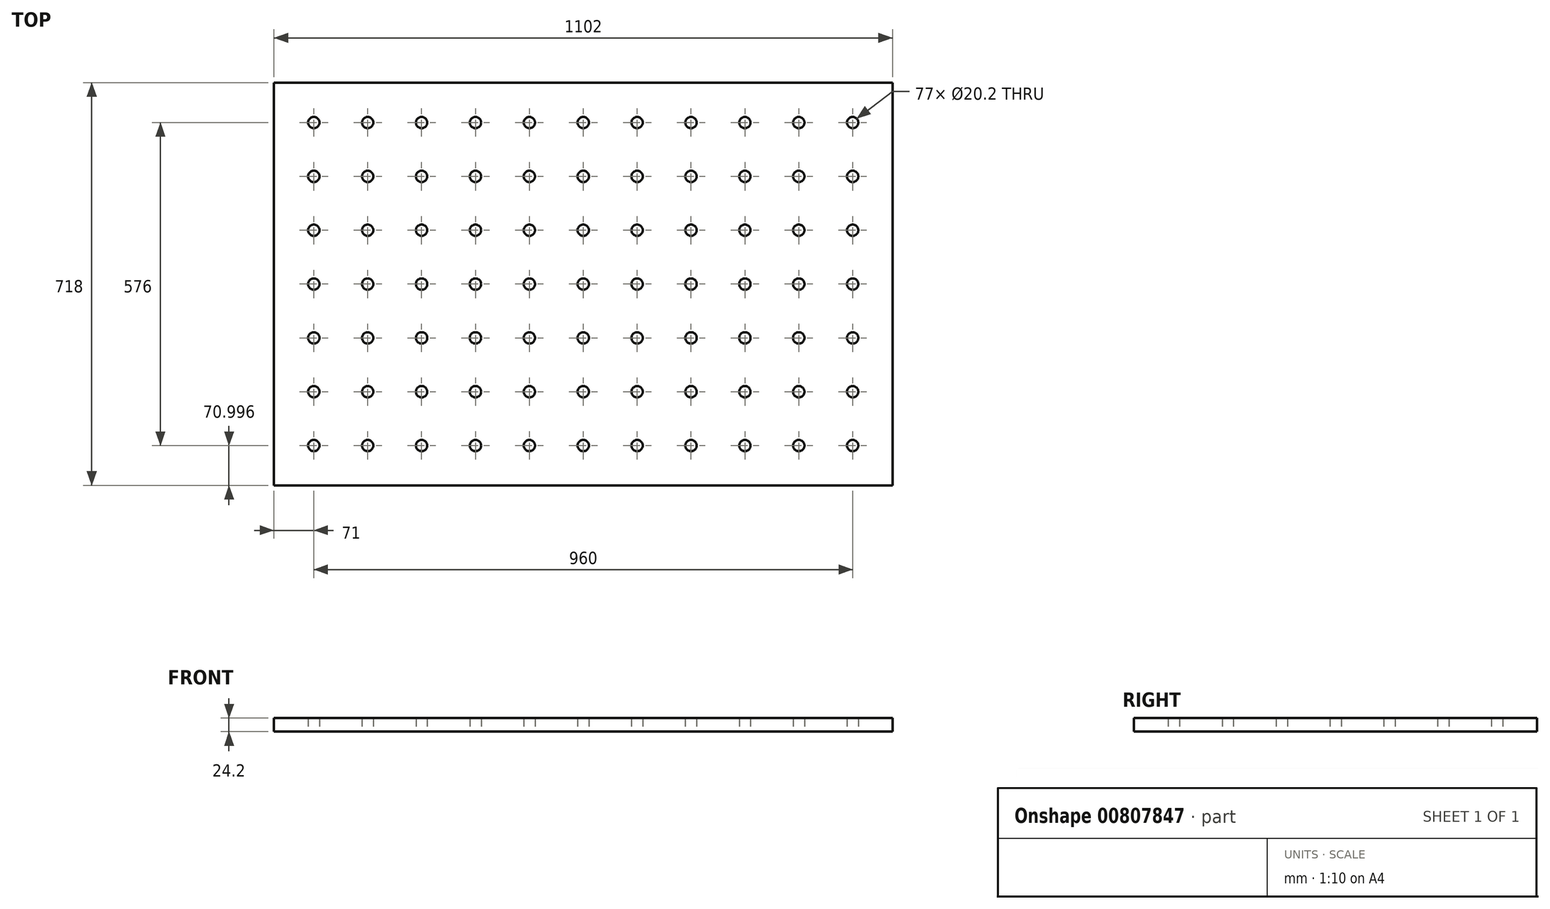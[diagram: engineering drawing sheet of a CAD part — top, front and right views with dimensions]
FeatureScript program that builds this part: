
annotation { "Feature Type Name" : "Feature", "Feature Type Description" : "" }
export const myFeature = defineFeature(function(context is Context, id is Id, definition is map)
    precondition{}
    {
        {
            var Q0;
            Q0=qCreatedBy(makeId("Top.planeOp"),FACE);
            var sketch = newSketch(context, id + "F0", { "sketchPlane" : qUnion([Q0])});
            skLineSegment(sketch, "E0.bottom", {"start": v(-588.77, 386.05) * mm, "end": v(513.23, 386.05) * mm});
            skLineSegment(sketch, "E0.top", {"start": v(-588.77, -331.95) * mm, "end": v(513.23, -331.95) * mm});
            skLineSegment(sketch, "E0.left", {"start": v(-588.77, 386.05) * mm, "end": v(-588.77, -331.95) * mm});
            skLineSegment(sketch, "E0.right", {"start": v(513.23, 386.05) * mm, "end": v(513.23, -331.95) * mm});
            skCircle(sketch, "E1", {"center": v(-517.77, 315.05) * mm, "radius": 10.1 * mm});
            skCircle(sketch, "E2.0.1.0", {"center": v(-517.77, 219.05) * mm, "radius": 10.1 * mm});
            skCircle(sketch, "E2.0.2.0", {"center": v(-517.77, 123.05) * mm, "radius": 10.1 * mm});
            skCircle(sketch, "E2.0.3.0", {"center": v(-517.77, 27.05) * mm, "radius": 10.1 * mm});
            skCircle(sketch, "E2.0.4.0", {"center": v(-517.77, -68.95) * mm, "radius": 10.1 * mm});
            skCircle(sketch, "E2.0.5.0", {"center": v(-517.77, -164.95) * mm, "radius": 10.1 * mm});
            skCircle(sketch, "E2.0.6.0", {"center": v(-517.77, -260.95) * mm, "radius": 10.1 * mm});
            skCircle(sketch, "E2.1.0.0", {"center": v(-421.77, 315.05) * mm, "radius": 10.1 * mm});
            skCircle(sketch, "E2.1.1.0", {"center": v(-421.77, 219.05) * mm, "radius": 10.1 * mm});
            skCircle(sketch, "E2.1.2.0", {"center": v(-421.77, 123.05) * mm, "radius": 10.1 * mm});
            skCircle(sketch, "E2.1.3.0", {"center": v(-421.77, 27.05) * mm, "radius": 10.1 * mm});
            skCircle(sketch, "E2.1.4.0", {"center": v(-421.77, -68.95) * mm, "radius": 10.1 * mm});
            skCircle(sketch, "E2.1.5.0", {"center": v(-421.77, -164.95) * mm, "radius": 10.1 * mm});
            skCircle(sketch, "E2.1.6.0", {"center": v(-421.77, -260.95) * mm, "radius": 10.1 * mm});
            skCircle(sketch, "E2.2.0.0", {"center": v(-325.77, 315.05) * mm, "radius": 10.1 * mm});
            skCircle(sketch, "E2.2.1.0", {"center": v(-325.77, 219.05) * mm, "radius": 10.1 * mm});
            skCircle(sketch, "E2.2.2.0", {"center": v(-325.77, 123.05) * mm, "radius": 10.1 * mm});
            skCircle(sketch, "E2.2.3.0", {"center": v(-325.77, 27.05) * mm, "radius": 10.1 * mm});
            skCircle(sketch, "E2.2.4.0", {"center": v(-325.77, -68.95) * mm, "radius": 10.1 * mm});
            skCircle(sketch, "E2.2.5.0", {"center": v(-325.77, -164.95) * mm, "radius": 10.1 * mm});
            skCircle(sketch, "E2.2.6.0", {"center": v(-325.77, -260.95) * mm, "radius": 10.1 * mm});
            skCircle(sketch, "E2.3.0.0", {"center": v(-229.77, 315.05) * mm, "radius": 10.1 * mm});
            skCircle(sketch, "E2.3.1.0", {"center": v(-229.77, 219.05) * mm, "radius": 10.1 * mm});
            skCircle(sketch, "E2.3.2.0", {"center": v(-229.77, 123.05) * mm, "radius": 10.1 * mm});
            skCircle(sketch, "E2.3.3.0", {"center": v(-229.77, 27.05) * mm, "radius": 10.1 * mm});
            skCircle(sketch, "E2.3.4.0", {"center": v(-229.77, -68.95) * mm, "radius": 10.1 * mm});
            skCircle(sketch, "E2.3.5.0", {"center": v(-229.77, -164.95) * mm, "radius": 10.1 * mm});
            skCircle(sketch, "E2.3.6.0", {"center": v(-229.77, -260.95) * mm, "radius": 10.1 * mm});
            skCircle(sketch, "E2.4.0.0", {"center": v(-133.77, 315.05) * mm, "radius": 10.1 * mm});
            skCircle(sketch, "E2.4.1.0", {"center": v(-133.77, 219.05) * mm, "radius": 10.1 * mm});
            skCircle(sketch, "E2.4.2.0", {"center": v(-133.77, 123.05) * mm, "radius": 10.1 * mm});
            skCircle(sketch, "E2.4.3.0", {"center": v(-133.77, 27.05) * mm, "radius": 10.1 * mm});
            skCircle(sketch, "E2.4.4.0", {"center": v(-133.77, -68.95) * mm, "radius": 10.1 * mm});
            skCircle(sketch, "E2.4.5.0", {"center": v(-133.77, -164.95) * mm, "radius": 10.1 * mm});
            skCircle(sketch, "E2.4.6.0", {"center": v(-133.77, -260.95) * mm, "radius": 10.1 * mm});
            skCircle(sketch, "E2.5.0.0", {"center": v(-37.77, 315.05) * mm, "radius": 10.1 * mm});
            skCircle(sketch, "E2.5.1.0", {"center": v(-37.77, 219.05) * mm, "radius": 10.1 * mm});
            skCircle(sketch, "E2.5.2.0", {"center": v(-37.77, 123.05) * mm, "radius": 10.1 * mm});
            skCircle(sketch, "E2.5.3.0", {"center": v(-37.77, 27.05) * mm, "radius": 10.1 * mm});
            skCircle(sketch, "E2.5.4.0", {"center": v(-37.77, -68.95) * mm, "radius": 10.1 * mm});
            skCircle(sketch, "E2.5.5.0", {"center": v(-37.77, -164.95) * mm, "radius": 10.1 * mm});
            skCircle(sketch, "E2.5.6.0", {"center": v(-37.77, -260.95) * mm, "radius": 10.1 * mm});
            skCircle(sketch, "E2.6.0.0", {"center": v(58.23, 315.05) * mm, "radius": 10.1 * mm});
            skCircle(sketch, "E2.6.1.0", {"center": v(58.23, 219.05) * mm, "radius": 10.1 * mm});
            skCircle(sketch, "E2.6.2.0", {"center": v(58.23, 123.05) * mm, "radius": 10.1 * mm});
            skCircle(sketch, "E2.6.3.0", {"center": v(58.23, 27.05) * mm, "radius": 10.1 * mm});
            skCircle(sketch, "E2.6.4.0", {"center": v(58.23, -68.95) * mm, "radius": 10.1 * mm});
            skCircle(sketch, "E2.6.5.0", {"center": v(58.23, -164.95) * mm, "radius": 10.1 * mm});
            skCircle(sketch, "E2.6.6.0", {"center": v(58.23, -260.95) * mm, "radius": 10.1 * mm});
            skCircle(sketch, "E2.7.0.0", {"center": v(154.23, 315.05) * mm, "radius": 10.1 * mm});
            skCircle(sketch, "E2.7.1.0", {"center": v(154.23, 219.05) * mm, "radius": 10.1 * mm});
            skCircle(sketch, "E2.7.2.0", {"center": v(154.23, 123.05) * mm, "radius": 10.1 * mm});
            skCircle(sketch, "E2.7.3.0", {"center": v(154.23, 27.05) * mm, "radius": 10.1 * mm});
            skCircle(sketch, "E2.7.4.0", {"center": v(154.23, -68.95) * mm, "radius": 10.1 * mm});
            skCircle(sketch, "E2.7.5.0", {"center": v(154.23, -164.95) * mm, "radius": 10.1 * mm});
            skCircle(sketch, "E2.7.6.0", {"center": v(154.23, -260.95) * mm, "radius": 10.1 * mm});
            skCircle(sketch, "E2.8.0.0", {"center": v(250.23, 315.05) * mm, "radius": 10.1 * mm});
            skCircle(sketch, "E2.8.1.0", {"center": v(250.23, 219.05) * mm, "radius": 10.1 * mm});
            skCircle(sketch, "E2.8.2.0", {"center": v(250.23, 123.05) * mm, "radius": 10.1 * mm});
            skCircle(sketch, "E2.8.3.0", {"center": v(250.23, 27.05) * mm, "radius": 10.1 * mm});
            skCircle(sketch, "E2.8.4.0", {"center": v(250.23, -68.95) * mm, "radius": 10.1 * mm});
            skCircle(sketch, "E2.8.5.0", {"center": v(250.23, -164.95) * mm, "radius": 10.1 * mm});
            skCircle(sketch, "E2.8.6.0", {"center": v(250.23, -260.95) * mm, "radius": 10.1 * mm});
            skCircle(sketch, "E2.9.0.0", {"center": v(346.23, 315.05) * mm, "radius": 10.1 * mm});
            skCircle(sketch, "E2.9.1.0", {"center": v(346.23, 219.05) * mm, "radius": 10.1 * mm});
            skCircle(sketch, "E2.9.2.0", {"center": v(346.23, 123.05) * mm, "radius": 10.1 * mm});
            skCircle(sketch, "E2.9.3.0", {"center": v(346.23, 27.05) * mm, "radius": 10.1 * mm});
            skCircle(sketch, "E2.9.4.0", {"center": v(346.23, -68.95) * mm, "radius": 10.1 * mm});
            skCircle(sketch, "E2.9.5.0", {"center": v(346.23, -164.95) * mm, "radius": 10.1 * mm});
            skCircle(sketch, "E2.9.6.0", {"center": v(346.23, -260.95) * mm, "radius": 10.1 * mm});
            skCircle(sketch, "E2.10.0.0", {"center": v(442.23, 315.05) * mm, "radius": 10.1 * mm});
            skCircle(sketch, "E2.10.1.0", {"center": v(442.23, 219.05) * mm, "radius": 10.1 * mm});
            skCircle(sketch, "E2.10.2.0", {"center": v(442.23, 123.05) * mm, "radius": 10.1 * mm});
            skCircle(sketch, "E2.10.3.0", {"center": v(442.23, 27.05) * mm, "radius": 10.1 * mm});
            skCircle(sketch, "E2.10.4.0", {"center": v(442.23, -68.95) * mm, "radius": 10.1 * mm});
            skCircle(sketch, "E2.10.5.0", {"center": v(442.23, -164.95) * mm, "radius": 10.1 * mm});
            skCircle(sketch, "E2.10.6.0", {"center": v(442.23, -260.95) * mm, "radius": 10.1 * mm});
            skLineSegment(sketch, "E2.direction1", {"start": v(-517.77, 315.05) * mm, "end": v(-421.77, 315.05) * mm, "construction": true});
            skLineSegment(sketch, "E2.direction2", {"start": v(-517.77, 315.05) * mm, "end": v(-517.77, 219.05) * mm, "construction": true});
            skSolve(sketch);
        }
        {
            var Q0;
            Q0=makeQuery(id+"F0.imprint","IMPRINT",FACE,{"disambiguationData":[TD([[makeQuery(id+"F0.imprint","IMPRINT",EDGE,{"derivedFrom":sQuery(id+"F0.wireOp",EDGE,"E0.bottom")}),-1.0]])]});
            extrude(context, id + "F1", {"entities" : qUnion([Q0]), "depth" : 24.2 * mm});
        }
    });
